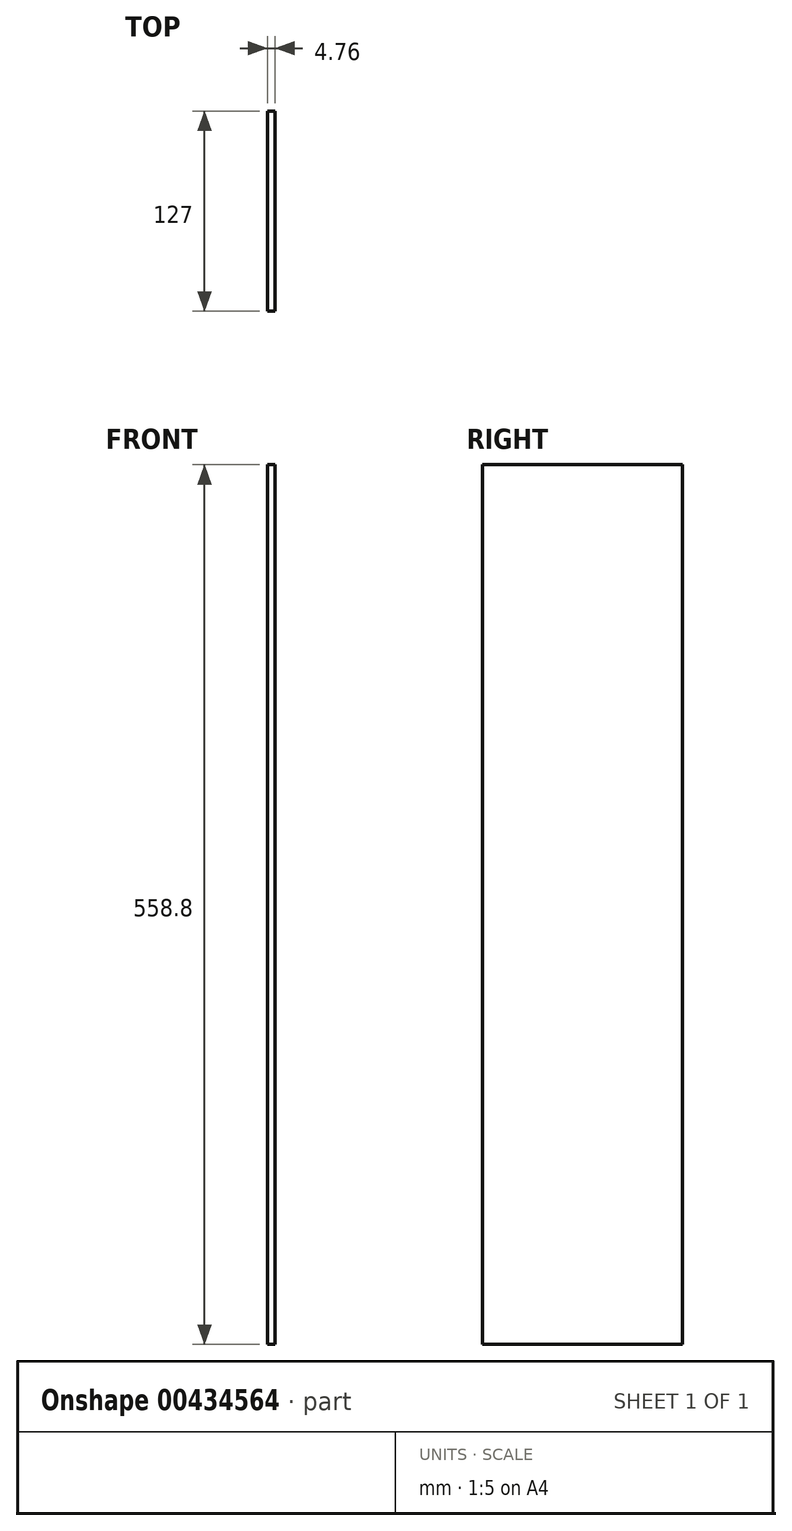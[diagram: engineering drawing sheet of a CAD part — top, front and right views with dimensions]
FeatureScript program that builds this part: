
annotation { "Feature Type Name" : "Feature", "Feature Type Description" : "" }
export const myFeature = defineFeature(function(context is Context, id is Id, definition is map)
    precondition{}
    {
        {
            var Q0;
            Q0=qCreatedBy(makeId("Right.planeOp"),FACE);
            var sketch = newSketch(context, id + "F0", { "sketchPlane" : qUnion([Q0])});
            skLineSegment(sketch, "E0.bottom", {"start": v(-93.48, 523.08) * mm, "end": v(33.52, 523.08) * mm});
            skLineSegment(sketch, "E0.top", {"start": v(-93.48, -35.72) * mm, "end": v(33.52, -35.72) * mm});
            skLineSegment(sketch, "E0.left", {"start": v(-93.48, 523.08) * mm, "end": v(-93.48, -35.72) * mm});
            skLineSegment(sketch, "E0.right", {"start": v(33.52, 523.08) * mm, "end": v(33.52, -35.72) * mm});
            skSolve(sketch);
        }
        {
            var Q0;
            Q0=makeQuery(id+"F0.imprint","IMPRINT",FACE,{"disambiguationData":[TD([[makeQuery(id+"F0.imprint","IMPRINT",EDGE,{"derivedFrom":sQuery(id+"F0.wireOp",EDGE,"E0.bottom")}),-1.0]])]});
            extrude(context, id + "F1", {"entities" : qUnion([Q0]), "depth" : 4.76 * mm});
        }
    });
